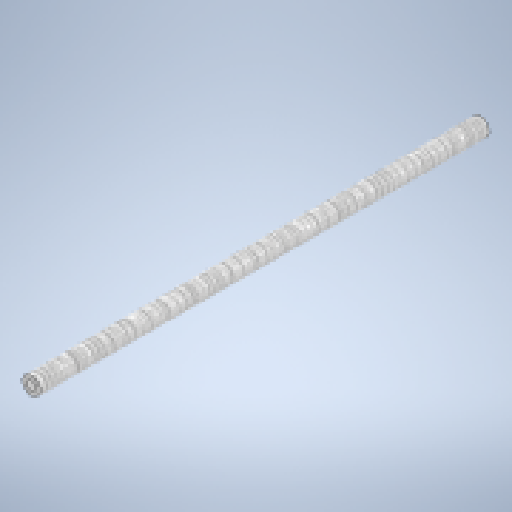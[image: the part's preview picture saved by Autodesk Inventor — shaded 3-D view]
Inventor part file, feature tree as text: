
AUTODESK INVENTOR PART (.ipt)
format: ipt  version: 2023.1 (Build 271208000, 208)  size: 266,240 bytes
history: native  units: mm
features: other x1, extrude x1, sketch x1
ambient origin geometry x8: Origin, YZ Plane, XZ Plane, XY Plane, X Axis, Y Axis, Z Axis, Center Point
bodies: Body1 (feature_tree)
feature tree (3):
  other  "ソリッド1"
  extrude  "押し出し1"  Depth=4.0mm
  sketch  "スケッチ1"
